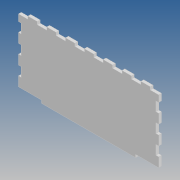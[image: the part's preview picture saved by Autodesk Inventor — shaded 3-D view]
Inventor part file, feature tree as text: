
AUTODESK INVENTOR PART (.ipt)
format: ipt  version: 2020 (Build 240168000, 168)  size: 154,112 bytes
history: native  units: mm
features: extrude x4, sketch x4, pattern_linear x2, other x1, mirror x1
ambient origin geometry x8: Origin, YZ Plane, XZ Plane, XY Plane, X Axis, Y Axis, Z Axis, Center Point
bodies: Body1 (feature_tree)
feature tree (12):
  other  "Твердое тело1"
  extrude  "Выдавливание1"  Depth=149.0mm
  extrude  "Выдавливание2"  Depth=70.0mm
  pattern_linear  "Прямоуг.массив1"  Spacing1=3.0mm  [1 undecoded]
  mirror  "Зеркальное отражение1"
  extrude  "Выдавливание3"  Depth=3.0mm
  extrude  "Выдавливание4"  Depth=10.0mm
  pattern_linear  "Прямоуг.массив2"  Spacing1=10.0mm  [1 undecoded]
  sketch  "Эскиз1"
  sketch  "Эскиз2"
  sketch  "Эскиз3"
  sketch  "Эскиз4"
note: 2 required parameter values undecoded (feature->parameter linkage not recoverable at this tier; creation-order binding heuristic only, values carry confidence <= 0.55)
